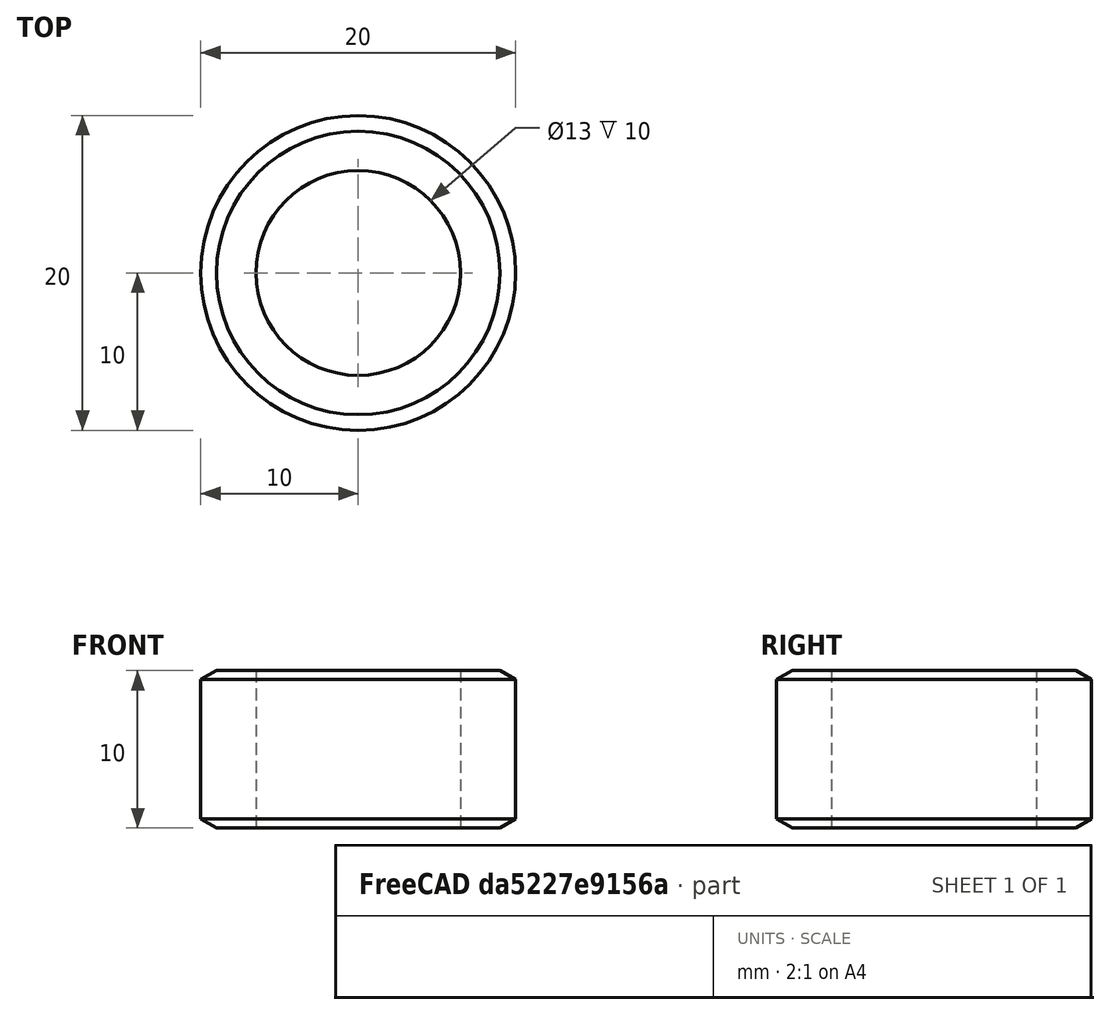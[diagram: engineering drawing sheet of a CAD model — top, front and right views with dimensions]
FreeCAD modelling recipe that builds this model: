
FCSTD DOCUMENT  (FreeCAD 0.16R5653 (Git))
Label: Shaft-washer-27
License: All rights reserved
LicenseURL: http://en.wikipedia.org/wiki/All_rights_reserved
objects: Sketcher::SketchObject×1, PartDesign::Revolution×1
note: 3 computed .brp shape members not serialized (recipe doc carries the construction recipe); baked Part::Feature solids carry a one-line shape summary decoded from their .brp

FEATURE [Sketcher::SketchObject] Sketch
  Placement = pos=(0,0,0) rot=(-1,0,0;4.71239rad)
  sketch-geometry (6):
    g0: LineSegment StartX=6.5 StartY=5 StartZ=0 EndX=6.5 EndY=-5 EndZ=0
    g1: LineSegment StartX=6.5 StartY=-5 StartZ=0 EndX=9 EndY=-5 EndZ=0
    g2: LineSegment StartX=9 StartY=-5 StartZ=0 EndX=10 EndY=-4.42265 EndZ=0
    g3: LineSegment StartX=10 StartY=-4.42265 StartZ=0 EndX=10 EndY=4.42265 EndZ=0
    g4: LineSegment StartX=10 StartY=4.42265 StartZ=0 EndX=9 EndY=5 EndZ=0
    g5: LineSegment StartX=9 StartY=5 StartZ=0 EndX=6.5 EndY=5 EndZ=0
  constraints (18):
    c: Vertical(g0)
    c: Coincident(g0,g1)
    c: Horizontal(g1)
    c: Coincident(g1,g2)
    c: Coincident(g2,g3)
    c: Vertical(g3)
    c: Coincident(g3,g4)
    c: Coincident(g4,g5)
    c: Coincident(g0,g5)
    c: Horizontal(g5)
    c: Angle(g5,g4) = 2.61799
    c: Angle(g2,g1) = 2.61799
    c: DistanceX(g-1,g0) = 6.5
    c: Symmetric(g2,g3,g-1)
    c: Symmetric(g0,g0,g-1)
    c: DistanceX(g-1,g2) = 10
    c: DistanceY(g0,g0) = 10
    c: DistanceX(g1) = 9
FEATURE [PartDesign::Revolution] Revolution
  Angle = 360
  Axis = (0,0,1)
  Base = (0,0,0)
  Placement = pos=(0,0,0) rot=(-1,0,0;4.71239rad)
  ReferenceAxis = -> Sketch [V_Axis]
  Reversed = true
  Sketch = -> Sketch
